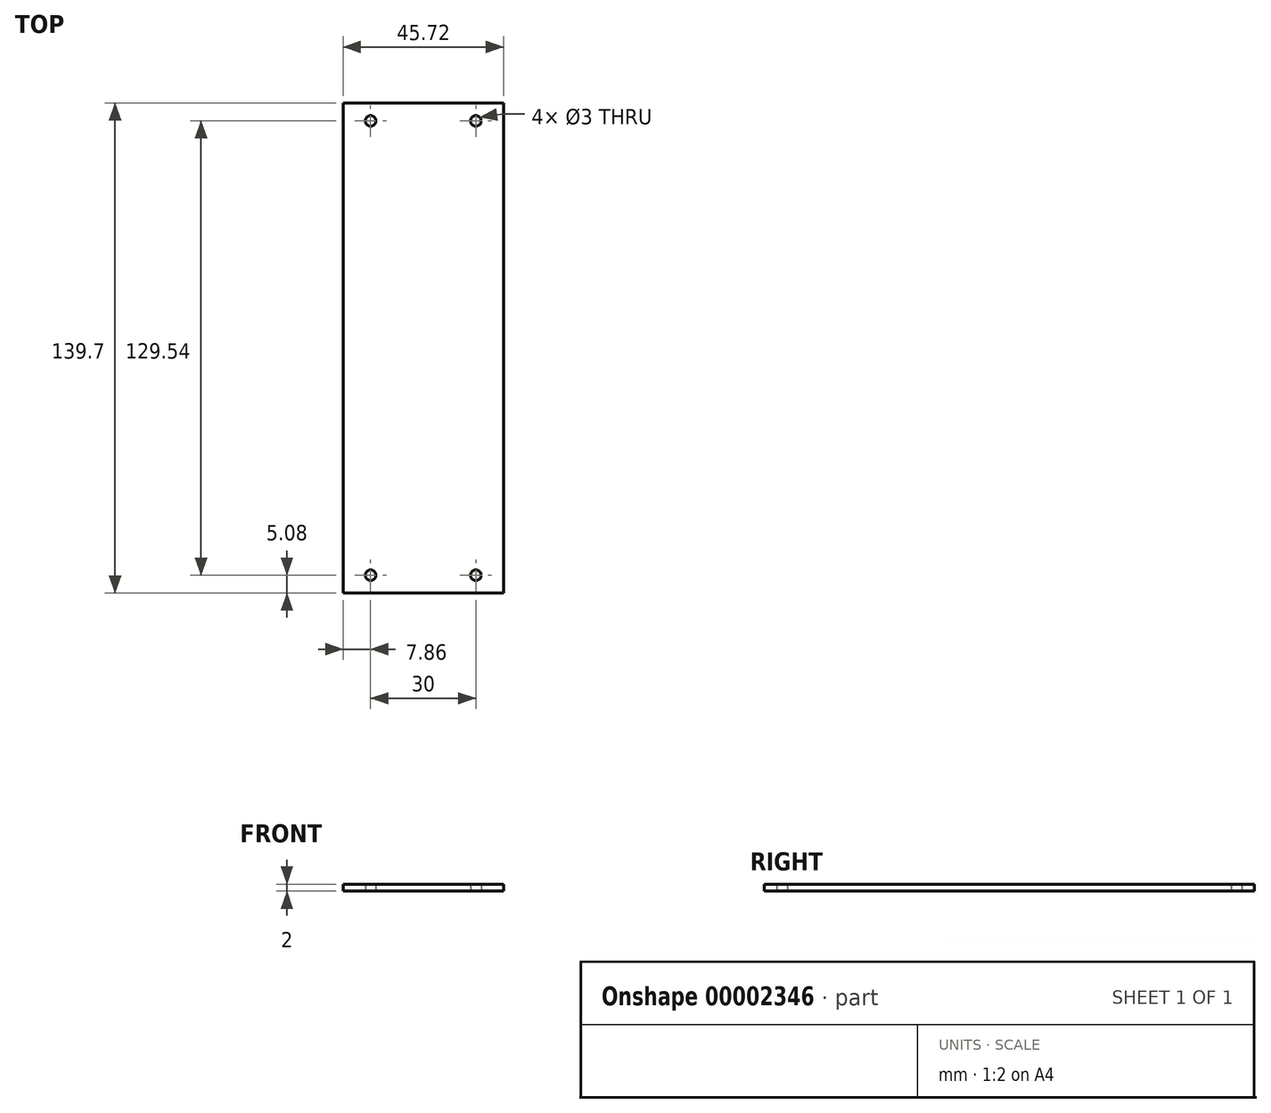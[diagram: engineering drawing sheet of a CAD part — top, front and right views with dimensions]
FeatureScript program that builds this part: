
annotation { "Feature Type Name" : "Feature", "Feature Type Description" : "" }
export const myFeature = defineFeature(function(context is Context, id is Id, definition is map)
    precondition{}
    {
        {
            var Q0;
            Q0=qCreatedBy(makeId("Top.planeOp"),FACE);
            var sketch = newSketch(context, id + "F0", { "sketchPlane" : qUnion([Q0])});
            skLineSegment(sketch, "E0.rect.bottom", {"start": v(22.86, 69.85) * mm, "end": v(-22.86, 69.85) * mm});
            skLineSegment(sketch, "E0.rect.top", {"start": v(22.86, -69.85) * mm, "end": v(-22.86, -69.85) * mm});
            skLineSegment(sketch, "E0.rect.left", {"start": v(22.86, 69.85) * mm, "end": v(22.86, -69.85) * mm});
            skLineSegment(sketch, "E0.rect.right", {"start": v(-22.86, 69.85) * mm, "end": v(-22.86, -69.85) * mm});
            skPoint(sketch, "E0.rect.middle", {"position": v(0, 0) * mm});
            skLineSegment(sketch, "E1", {"start": v(0, 64.77) * mm, "end": v(15, 64.77) * mm, "construction": true});
            skLineSegment(sketch, "E2", {"start": v(15, 64.77) * mm, "end": v(15, 69.85) * mm, "construction": true});
            skCircle(sketch, "E3", {"center": v(15, 64.77) * mm, "radius": 1.5 * mm});
            skCircle(sketch, "E4.0.MirrorC", {"center": v(-15, 64.77) * mm, "radius": 1.5 * mm});
            skCircle(sketch, "E5.0.MirrorC", {"center": v(-15, -64.77) * mm, "radius": 1.5 * mm});
            skCircle(sketch, "E6.0.MirrorC", {"center": v(15, -64.77) * mm, "radius": 1.5 * mm});
            skSolve(sketch);
        }
        {
            var Q0;
            Q0=makeQuery(id+"F0.imprint","IMPRINT",FACE,{"disambiguationData":[TD([[makeQuery(id+"F0.imprint","IMPRINT",EDGE,{"derivedFrom":sQuery(id+"F0.wireOp",EDGE,"E0.rect.bottom")}),1.0]])]});
            extrude(context, id + "F1", {"entities" : qUnion([Q0]), "depth" : 2 * mm});
        }
    });
